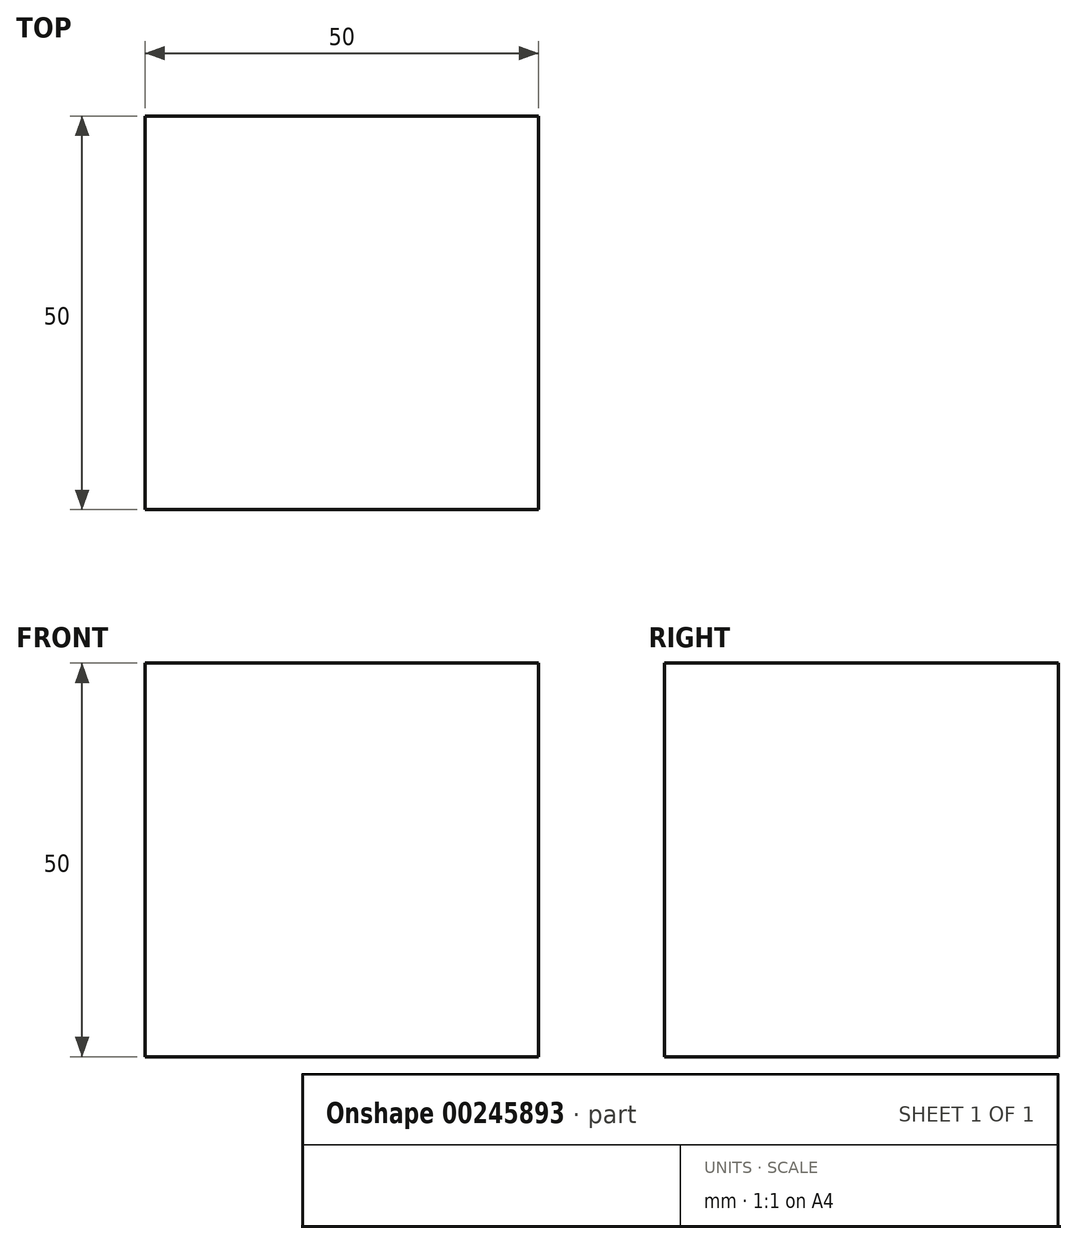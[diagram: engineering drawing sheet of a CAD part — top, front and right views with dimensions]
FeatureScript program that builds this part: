
annotation { "Feature Type Name" : "Feature", "Feature Type Description" : "" }
export const myFeature = defineFeature(function(context is Context, id is Id, definition is map)
    precondition{}
    {
        {
            var Q0;
            Q0=qCreatedBy(makeId("Front.planeOp"),FACE);
            var sketch = newSketch(context, id + "F0", { "sketchPlane" : qUnion([Q0])});
            skLineSegment(sketch, "E0.bottom", {"start": v(0, 0) * mm, "end": v(50, 0) * mm});
            skLineSegment(sketch, "E0.top", {"start": v(0, 50) * mm, "end": v(50, 50) * mm});
            skLineSegment(sketch, "E0.left", {"start": v(0, 0) * mm, "end": v(0, 50) * mm});
            skLineSegment(sketch, "E0.right", {"start": v(50, 0) * mm, "end": v(50, 50) * mm});
            skSolve(sketch);
        }
        {
            var Q0;
            Q0 = qSketchRegion(id + "F0", true);
            extrude(context, id + "F1", {"entities" : qUnion([Q0]), "depth" : 50 * mm});
        }
    });
